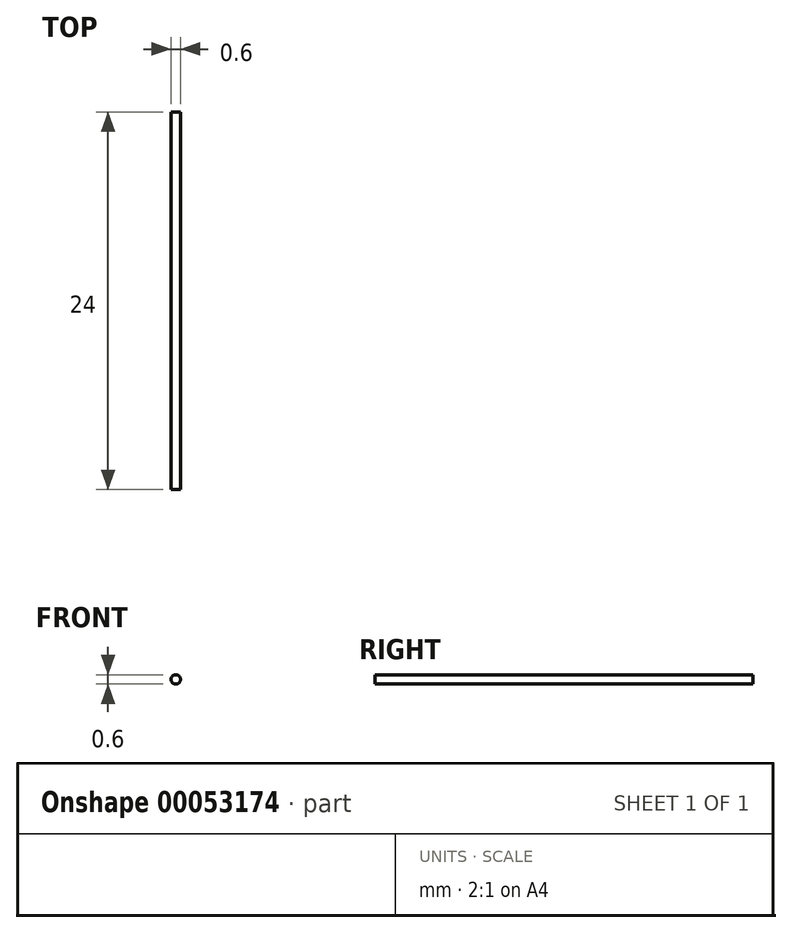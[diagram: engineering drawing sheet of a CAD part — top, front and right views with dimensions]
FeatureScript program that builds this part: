
annotation { "Feature Type Name" : "Feature", "Feature Type Description" : "" }
export const myFeature = defineFeature(function(context is Context, id is Id, definition is map)
    precondition{}
    {
        {
            var Q0;
            Q0=qCreatedBy(makeId("Front.planeOp"),FACE);
            var sketch = newSketch(context, id + "F0", { "sketchPlane" : qUnion([Q0])});
            skCircle(sketch, "E0", {"center": v(0, 0) * mm, "radius": 0.3 * mm});
            skSolve(sketch);
        }
        {
            var Q0;
            Q0=makeQuery(id+"F0.imprint","IMPRINT",FACE,{"disambiguationData":[TD([[makeQuery(id+"F0.imprint","IMPRINT",EDGE,{"derivedFrom":sQuery(id+"F0.wireOp",EDGE,"E0")}),1.0]])]});
            var Q1;
            Q1=sQuery(id+"F0.wireOp",EDGE,"E0");
            extrude(context, id + "F1", {"entities" : qUnion([Q0]), "surfaceEntities" : qUnion([Q1]), "depth" : 24 * mm});
        }
    });
